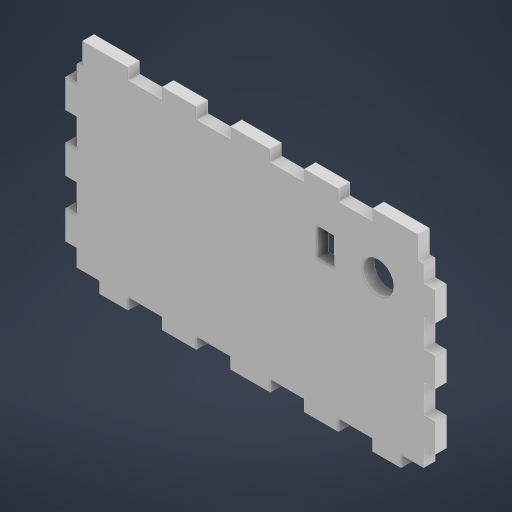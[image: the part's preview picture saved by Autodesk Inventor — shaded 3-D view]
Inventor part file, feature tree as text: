
AUTODESK INVENTOR PART (.ipt)
format: ipt  version: 2023.2 (Build 272271000, 271)  size: 378,368 bytes
history: native  units: mm
features: sketch x4
ambient origin geometry x8: Origin, YZ Plane, XZ Plane, XY Plane, X Axis, Y Axis, Z Axis, Center Point
bodies: Body1 (feature_tree)
feature tree (4):
  sketch  "Sketch1"  dims[d228=130.0mm]
  sketch  "Sketch2"  dims[d229=74.0mm]
  sketch  "Sketch3"  dims[d230=4.0mm d231=0.0mm]
  sketch  "Sketch4"  dims[d234=10.0mm d235=12.0mm d236=12.0mm d237=12.0mm d238=14.0mm d240=12.0mm d242=12.0mm d243=10.0mm d244=12.0mm d245=12.0mm d246=12.0mm d249=10.0mm d251=10.0mm d255=10.0mm d259=4.0mm d260=0.0mm d262=4.0mm d267=10.0mm d268=10.0mm d271=10.0mm d272=14.0mm d274=6.0mm d278=8.0mm d279=11.0mm d280=20.0mm d281=20.0mm d282=4.0mm d283=0.0mm d297=10.0mm d298=10.0mm d299=6.0mm d300=4.0mm d301=0.0mm d9=0.5mm d10=0.872665mm d11=0.5mm d12=0.872665mm d13=0.5mm d14=0.872665mm d27=0.5mm d28=0.872665mm d29=0.5mm d30=0.872665mm d88=0.5mm d89=0.872665mm d90=0.5mm d91=0.872665mm d116=0.5mm d117=0.872665mm d118=0.5mm d119=0.872665mm d154=0.5mm d155=0.872665mm d156=0.5mm d157=0.872665mm d181=0.5mm d182=0.872665mm d183=0.5mm d184=0.872665mm d221=0.5mm d222=0.872665mm d223=0.5mm d224=0.872665mm]
